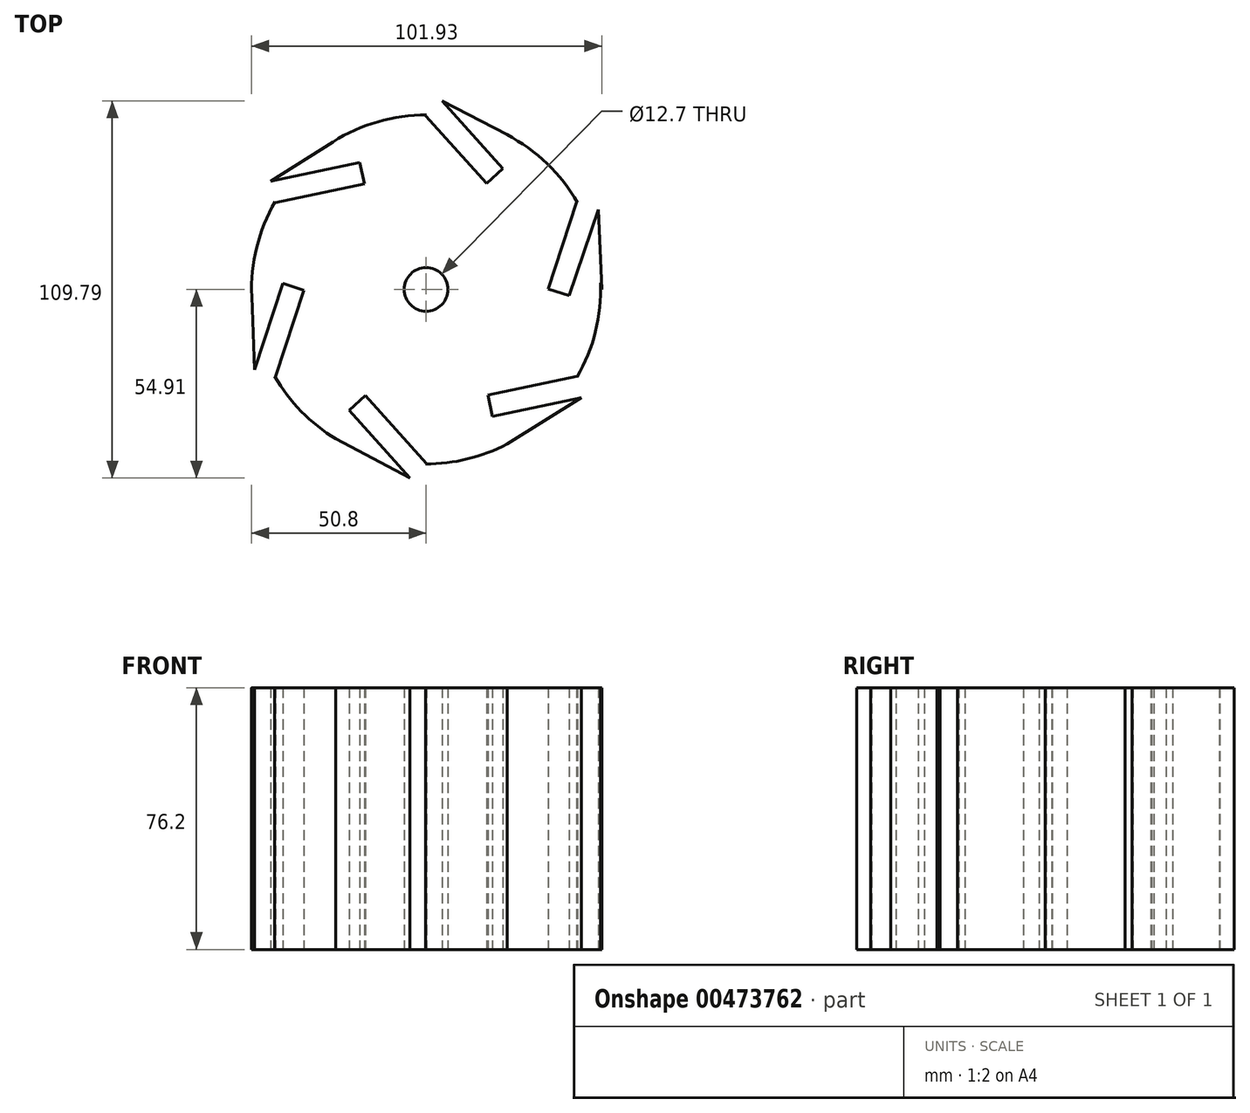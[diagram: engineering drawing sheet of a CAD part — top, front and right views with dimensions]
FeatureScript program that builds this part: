
annotation { "Feature Type Name" : "Feature", "Feature Type Description" : "" }
export const myFeature = defineFeature(function(context is Context, id is Id, definition is map)
    precondition{}
    {
        {
            var Q0;
            Q0=qCreatedBy(makeId("Top.planeOp"),FACE);
            var sketch = newSketch(context, id + "F0", { "sketchPlane" : qUnion([Q0])});
            skArc(sketch, "E0", {"start": v(-44.06, -25.28) * mm, "mid": v(-34.3, -37.48) * mm, "end": v(-21.28, -46.13) * mm});
            skPoint(sketch, "E1.0.midPoint", {"position": v(21.84, 37.96) * mm});
            skPoint(sketch, "E2.0.midPoint", {"position": v(-26.77, 15.25) * mm});
            skLineSegment(sketch, "E3", {"start": v(-43.87, 25.26) * mm, "end": v(-17.96, 30.7) * mm});
            skLineSegment(sketch, "E4", {"start": v(-17.96, 30.7) * mm, "end": v(-19.28, 37) * mm});
            skLineSegment(sketch, "E5", {"start": v(-43.87, 25.26) * mm, "end": v(-43.92, 25.52) * mm});
            skLineSegment(sketch, "E6", {"start": v(-45.2, 31.55) * mm, "end": v(-19.28, 37) * mm});
            skLineSegment(sketch, "E7", {"start": v(-0.1, 50.59) * mm, "end": v(17.58, 30.88) * mm});
            skLineSegment(sketch, "E8", {"start": v(43.77, 25.33) * mm, "end": v(35.54, 0.17) * mm});
            skLineSegment(sketch, "E9", {"start": v(43.87, -25.26) * mm, "end": v(17.96, -30.7) * mm});
            skLineSegment(sketch, "E10", {"start": v(0.06, -50.62) * mm, "end": v(-17.61, -30.9) * mm});
            skLineSegment(sketch, "E11", {"start": v(-43.8, -25.36) * mm, "end": v(-35.57, -0.2) * mm});
            skLineSegment(sketch, "E12", {"start": v(-0.1, 50.59) * mm, "end": v(0.14, 50.8) * mm});
            skLineSegment(sketch, "E13", {"start": v(43.77, 25.33) * mm, "end": v(44.1, 25.22) * mm});
            skLineSegment(sketch, "E14", {"start": v(43.87, -25.26) * mm, "end": v(43.92, -25.52) * mm});
            skLineSegment(sketch, "E15", {"start": v(0.06, -50.62) * mm, "end": v(-0.14, -50.8) * mm});
            skLineSegment(sketch, "E16", {"start": v(-43.8, -25.36) * mm, "end": v(-44.06, -25.28) * mm});
            skLineSegment(sketch, "E17", {"start": v(17.58, 30.88) * mm, "end": v(22.36, 35.16) * mm});
            skLineSegment(sketch, "E18", {"start": v(22.36, 35.16) * mm, "end": v(4.69, 54.88) * mm});
            skLineSegment(sketch, "E19", {"start": v(35.54, 0.17) * mm, "end": v(41.64, -1.83) * mm});
            skLineSegment(sketch, "E20", {"start": v(41.64, -1.83) * mm, "end": v(50.2, 23.23) * mm});
            skLineSegment(sketch, "E21", {"start": v(17.96, -30.7) * mm, "end": v(19.28, -37) * mm});
            skLineSegment(sketch, "E22", {"start": v(19.28, -37) * mm, "end": v(45.2, -31.55) * mm});
            skLineSegment(sketch, "E23", {"start": v(-17.61, -30.9) * mm, "end": v(-22.4, -35.2) * mm});
            skLineSegment(sketch, "E24", {"start": v(-22.4, -35.2) * mm, "end": v(-4.72, -54.9) * mm});
            skLineSegment(sketch, "E25", {"start": v(-35.57, -0.2) * mm, "end": v(-41.68, 1.8) * mm});
            skLineSegment(sketch, "E26", {"start": v(-41.68, 1.8) * mm, "end": v(-49.9, -23.37) * mm});
            skArc(sketch, "E27.trimOffspring", {"start": v(-43.92, 25.52) * mm, "mid": v(-49.3, 12.23) * mm, "end": v(-50.76, -2.03) * mm});
            skArc(sketch, "E28.trimOffspring", {"start": v(0.14, 50.8) * mm, "mid": v(-14.05, 48.82) * mm, "end": v(-27.12, 42.95) * mm});
            skArc(sketch, "E29.trimOffspring", {"start": v(44.1, 25.22) * mm, "mid": v(35.24, 36.6) * mm, "end": v(23.55, 45.01) * mm});
            skArc(sketch, "E30.trimOffspring", {"start": v(43.92, -25.52) * mm, "mid": v(49.3, -12.27) * mm, "end": v(50.76, 1.94) * mm});
            skArc(sketch, "E31.trimOffspring", {"start": v(-0.14, -50.8) * mm, "mid": v(15.7, -48.31) * mm, "end": v(29.98, -41.01) * mm});
            skLineSegment(sketch, "E32", {"start": v(-49.9, -23.37) * mm, "end": v(-50.84, 0) * mm});
            skLineSegment(sketch, "E33", {"start": v(-50.84, 0) * mm, "end": v(-50.37, -11.68) * mm});
            skLineSegment(sketch, "E34", {"start": v(50.2, 23.23) * mm, "end": v(51.13, 0) * mm});
            skLineSegment(sketch, "E35", {"start": v(45.2, -31.55) * mm, "end": v(23.55, -45.01) * mm});
            skLineSegment(sketch, "E36", {"start": v(-4.72, -54.9) * mm, "end": v(-26.25, -43.5) * mm});
            skLineSegment(sketch, "E37", {"start": v(-45.2, 31.55) * mm, "end": v(-26.25, 43.5) * mm});
            skLineSegment(sketch, "E38", {"start": v(4.69, 54.88) * mm, "end": v(26.43, 43.5) * mm});
            skLineSegment(sketch, "E39", {"start": v(51.13, 0) * mm, "end": v(50.76, 1.94) * mm});
            skCircle(sketch, "E40", {"center": v(0, 0) * mm, "radius": 6.35 * mm});
            skSolve(sketch);
        }
        {
            var Q0;
            Q0=makeQuery(id+"F0.imprint","IMPRINT",FACE,{"disambiguationData":[TD([[makeQuery(id+"F0.imprint","IMPRINT",EDGE,{"derivedFrom":sQuery(id+"F0.wireOp",EDGE,"E3")}),-1.0]])]});
            extrude(context, id + "F1", {"entities" : qUnion([Q0]), "depth" : 76.2 * mm});
        }
    });
